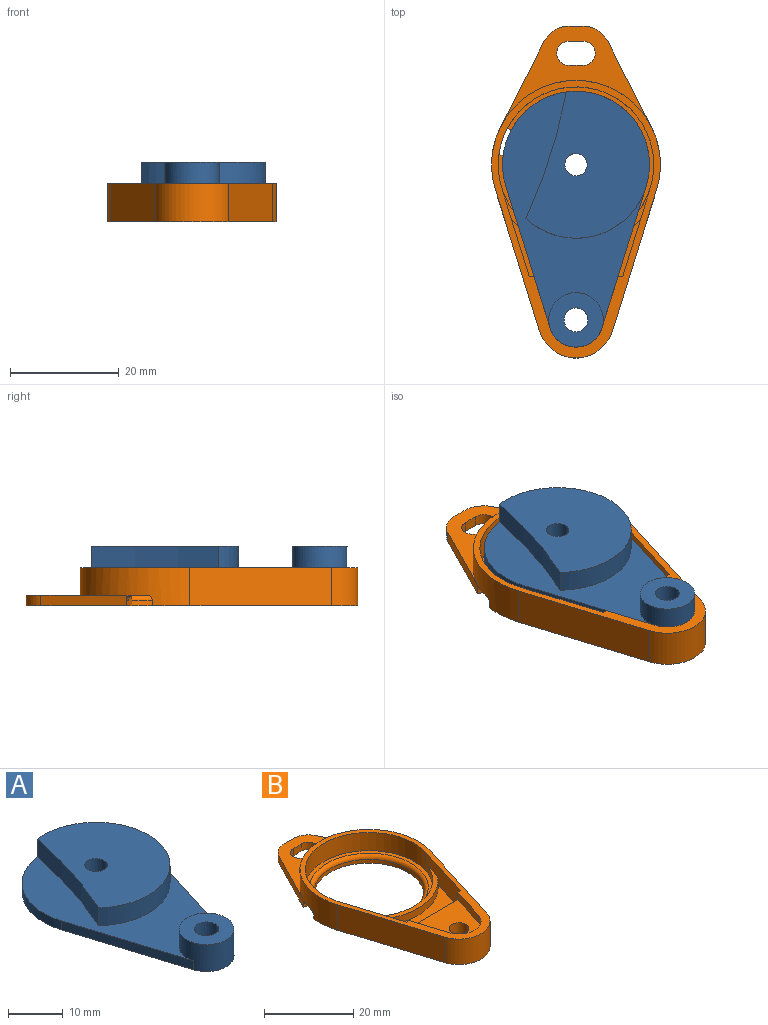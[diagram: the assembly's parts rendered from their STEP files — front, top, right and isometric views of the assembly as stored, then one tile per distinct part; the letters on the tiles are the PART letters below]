
ASSEMBLY  parts=2 mates=1
PART A: 11 faces, bbox 27x47x6 mm
  f0: plane 25.97x8.11mm, normal (0.95,-0.3,0), area 54.4mm2, adj f1,f4,f6,f7
  f1: cylinder r=13.5mm len=27mm, axis (0,0,1), area 318.3mm2, adj f0,f2,f6,f7,f8,f9
  f2: plane 25.97x8.11mm, normal (-0.95,-0.3,0), area 54.4mm2, adj f1,f4,f6,f7
  f3: cylinder r=2.05mm len=6mm, axis (0,0,1), area 77.3mm2, adj f6,f9
  f4: cylinder r=5mm len=10mm, axis (0,0,1), area 151mm2, adj f0,f2,f6,f7,f10
  f5: cylinder r=2.2mm len=6mm, axis (0,0,1), area 82.9mm2, adj f6,f10
  f6: plane 47x27mm, normal (0,0,-1), area 848mm2, adj f0,f1,f2,f3,f4,f5
  f7: plane 43.38x26.39mm, normal (0,0,1), area 373.4mm2, adj f0,f1,f2,f4,f8
  f8: cylinder r=100mm len=23.27mm, axis (0,0,-1), area 98mm2, adj f1,f7,f9
  f9: plane 27x22.7mm, normal (0,0,1), area 411.3mm2, adj f1,f3,f8
  f10: plane 10x10mm, normal (0,0,1), area 63.3mm2, adj f4,f5
PART B: 36 faces, bbox 31x61x7 mm
  f0: cylinder r=15.5mm len=31mm, axis (0,0,-1), area 328.8mm2, adj f1,f3,f12,f13,f20,f21,f29,f31
  f1: plane 61x31mm, normal (0,0,-1), area 756.6mm2, adj f0,f3,f4,f12,f15,f16,f20,f21
  f2: plane 28.6x28.6mm, normal (0,0,1), area 81.7mm2, adj f8,f19,f31,f33
  f3: plane 25.97x8.11mm, normal (-0.95,-0.3,0), area 190.4mm2, adj f0,f1,f4,f13
  f4: cylinder r=7mm len=13.36mm, axis (0,0,-1), area 124.3mm2, adj f1,f3,f12,f13
  f5: cylinder r=5mm len=9.55mm, axis (0,0,-1), area 25.4mm2, adj f6,f11,f13,f14
  f6: plane 9.51x2.97mm, normal (0.95,0.3,0), area 19.9mm2, adj f5,f10,f13,f14
  f7: plane 16.22x5.07mm, normal (0.95,0.3,0), area 73mm2, adj f8,f10,f13,f17,f18,f30
  f8: cylinder r=14.3mm len=28.6mm, axis (0,0,-1), area 340.9mm2, adj f2,f7,f9,f13,f18,f31,f32,f33
  f9: plane 16.22x5.07mm, normal (-0.95,0.3,0), area 73mm2, adj f8,f10,f13,f17,f18,f30
  f10: plane 17.16x5mm, normal (0,1,0), area 54.8mm2, adj f6,f7,f9,f11,f13,f14,f30
  f11: plane 9.51x2.97mm, normal (-0.95,0.3,0), area 19.9mm2, adj f5,f10,f13,f14
  f12: plane 25.97x8.11mm, normal (0.95,-0.3,0), area 190.4mm2, adj f0,f1,f4,f13
  f13: plane 51x31mm, normal (0,0,1), area 178.9mm2, adj f0,f3,f4,f5,f6,f7,f8,f9
  f14: plane 15.49x13.02mm, normal (0,0,1), area 128.4mm2, adj f5,f6,f10,f11,f15
  f15: cylinder r=2.2mm len=5mm, axis (0,0,1), area 69.1mm2, adj f1,f14
  f16: cylinder r=12.3mm len=24.6mm, axis (0,0,-1), area 72.2mm2, adj f1,f19,f31,f33
  f17: cylinder r=15.5mm len=23.73mm, axis (0,0,-1), area 54.1mm2, adj f7,f9,f18,f30
  f18: plane 27.3x11.24mm, normal (0,0,1), area 35.7mm2, adj f7,f8,f9,f17
  f19: torus R=13.3mm, axis (0,0,-1), area 117.1mm2, adj f2,f16,f31,f33
  f20: plane 15.71x8.02mm, normal (0.89,0.45,0), area 35.3mm2, adj f0,f1,f28,f29
  f21: plane 15.71x8.02mm, normal (-0.89,0.45,0), area 35.3mm2, adj f0,f1,f22,f29,f33
  f22: cylinder r=5mm len=4.32mm, axis (0,0,-1), area 10.7mm2, adj f1,f21,f23,f29
  f23: cylinder r=54mm len=2.95mm, axis (0,0,-1), area 5.9mm2, adj f1,f22,f28,f29
  f24: cylinder r=46.8mm len=2.55mm, axis (0,0,-1), area 5.1mm2, adj f1,f25,f27,f29
  f25: cylinder r=2.2mm len=4.4mm, axis (0,0,-1), area 13.8mm2, adj f1,f24,f26,f29
  f26: cylinder r=51.2mm len=2.79mm, axis (0,0,-1), area 5.6mm2, adj f1,f25,f27,f29
  f27: cylinder r=2.2mm len=4.4mm, axis (0,0,-1), area 13.8mm2, adj f1,f24,f26,f29
  f28: cylinder r=5mm len=4.32mm, axis (0,0,-1), area 10.7mm2, adj f1,f20,f23,f29
  f29: plane 27.61x18.46mm, normal (0,0,1), area 138.8mm2, adj f0,f20,f21,f22,f23,f24,f25,f26
  f30: plane 23.73x10.51mm, normal (0,0,1), area 123.8mm2, adj f7,f9,f10,f17
  f31: plane 3.1x2mm, normal (0.3,0.95,0), area 5.1mm2, adj f0,f1,f2,f8,f16,f19,f35
  f32: plane 3.23x2.06mm, normal (0,0,-1), area 3.6mm2, adj f0,f8,f34,f35
  f33: plane 3.1x2mm, normal (-0.3,-0.95,0), area 5.1mm2, adj f1,f2,f8,f16,f19,f21,f34
  f34: cylinder r=1mm len=1.59mm, axis (-0.95,0.3,0), area 1.9mm2, adj f0,f8,f32,f33
  f35: cylinder r=1mm len=1.59mm, axis (0.95,-0.3,0), area 1.9mm2, adj f0,f8,f31,f32
PLACE A t=(0,0,2)mm
PLACE B at identity
MATE fastened A.f5 <-> B.f15  axis (0,0,-1) through (0,-28.5,0)mm
